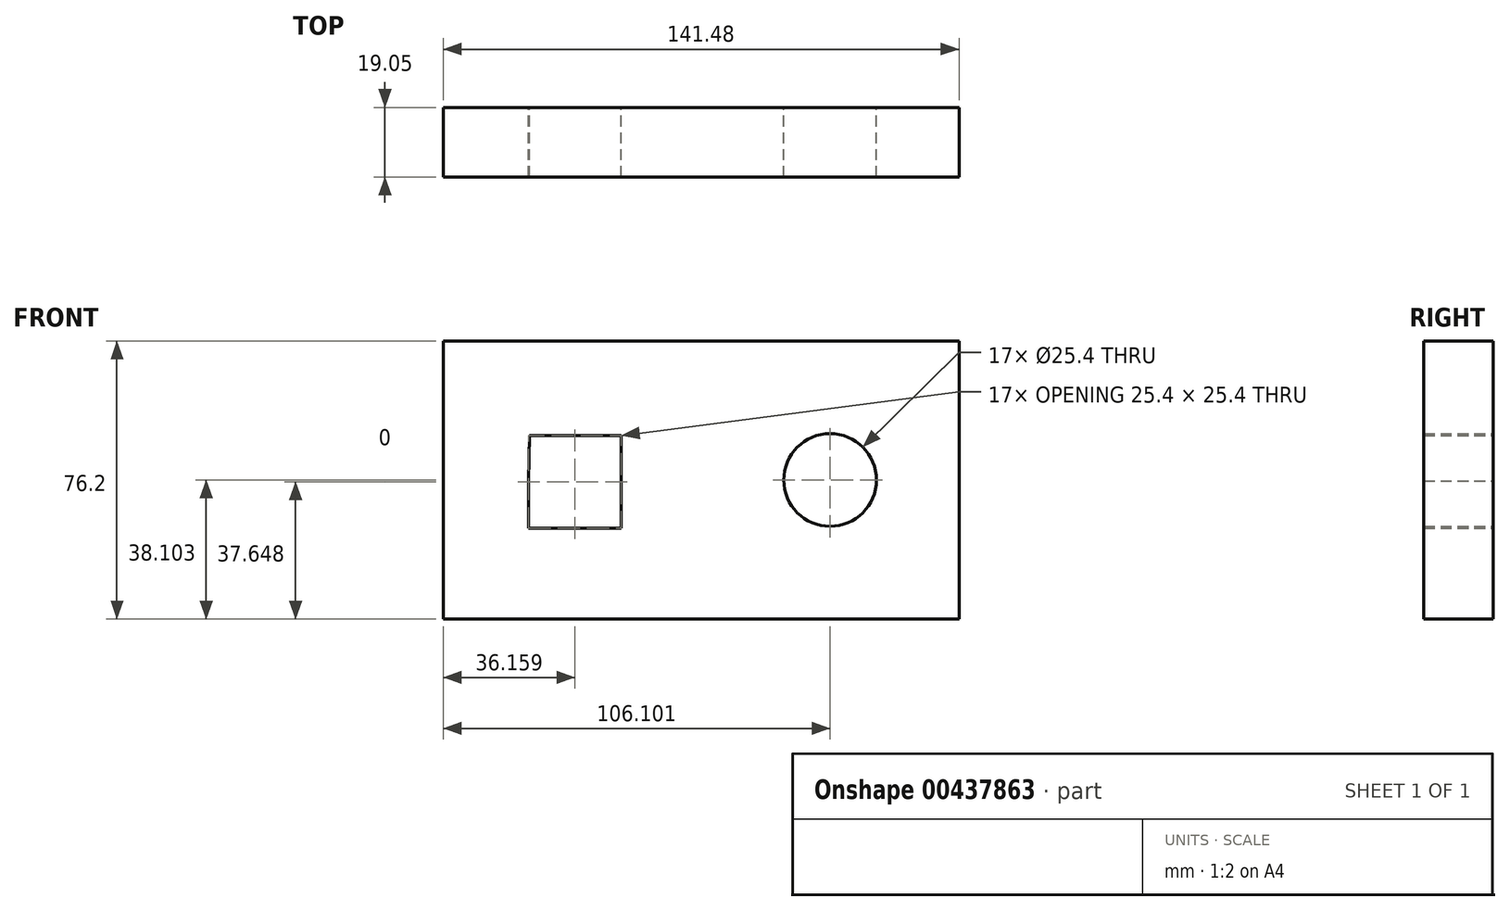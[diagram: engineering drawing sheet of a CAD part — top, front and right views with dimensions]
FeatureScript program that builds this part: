
annotation { "Feature Type Name" : "Feature", "Feature Type Description" : "" }
export const myFeature = defineFeature(function(context is Context, id is Id, definition is map)
    precondition{}
    {
        {
            var Q0;
            Q0=qCreatedBy(makeId("Front.planeOp"),FACE);
            var sketch = newSketch(context, id + "F0", { "sketchPlane" : qUnion([Q0])});
            skLineSegment(sketch, "E0", {"start": v(-73.29, 60.14) * mm, "end": v(68.2, 60.14) * mm});
            skPoint(sketch, "E1.start.orphan", {"position": v(-73.29, 47.35) * mm});
            skLineSegment(sketch, "E2", {"start": v(-73.29, 60.14) * mm, "end": v(-73.29, -16.06) * mm});
            skLineSegment(sketch, "E3", {"start": v(-73.29, -16.06) * mm, "end": v(-2.55, -16.06) * mm});
            skLineSegment(sketch, "E4", {"start": v(68.2, 60.14) * mm, "end": v(68.2, -16.06) * mm});
            skPoint(sketch, "E5.endSnap0", {"position": v(-3.02, -16.06) * mm});
            skPoint(sketch, "E6.end.orphan", {"position": v(-73.29, -21.4) * mm});
            skPoint(sketch, "E6.start.orphan", {"position": v(-2.55, -21.4) * mm});
            skPoint(sketch, "E7.orphan", {"position": v(-37.93, 0) * mm});
            skPoint(sketch, "E8.end.orphan", {"position": v(-40.56, 22.04) * mm});
            skPoint(sketch, "E9.trimOffspring.end.orphan", {"position": v(-73.29, 22.04) * mm});
            skPoint(sketch, "E10.end.orphan", {"position": v(-37.93, -21.4) * mm});
            skLineSegment(sketch, "E11", {"start": v(-37.13, 34.29) * mm, "end": v(-24.43, 34.29) * mm});
            skLineSegment(sketch, "E12", {"start": v(-24.43, 21.59) * mm, "end": v(-24.43, 34.29) * mm});
            skLineSegment(sketch, "E13", {"start": v(-37.13, 34.29) * mm, "end": v(-49.6, 34.29) * mm});
            skLineSegment(sketch, "E14", {"start": v(-49.83, 21.82) * mm, "end": v(-49.6, 34.29) * mm});
            skLineSegment(sketch, "E15", {"start": v(-37.13, 8.89) * mm, "end": v(-49.83, 8.89) * mm});
            skLineSegment(sketch, "E16", {"start": v(-49.83, 21.82) * mm, "end": v(-49.83, 8.89) * mm});
            skLineSegment(sketch, "E17", {"start": v(-24.43, 21.59) * mm, "end": v(-24.43, 8.89) * mm});
            skLineSegment(sketch, "E18", {"start": v(-37.13, 8.89) * mm, "end": v(-24.43, 8.89) * mm});
            skPoint(sketch, "E19.orphan", {"position": v(67.25, -16.06) * mm});
            skLineSegment(sketch, "E20", {"start": v(-2.55, -16.06) * mm, "end": v(68.2, -16.06) * mm});
            skCircle(sketch, "E21", {"center": v(32.81, 22.04) * mm, "radius": 12.7 * mm});
            skPoint(sketch, "E22.orphan", {"position": v(-2.55, 60.14) * mm});
            skPoint(sketch, "E23.orphan", {"position": v(68.2, 22.04) * mm});
            skSolve(sketch);
        }
        {
            var Q0;
            Q0=makeQuery(id+"F0.imprint","IMPRINT",FACE,{"disambiguationData":[TD([[makeQuery(id+"F0.imprint","IMPRINT",EDGE,{"derivedFrom":sQuery(id+"F0.wireOp",EDGE,"E0")}),-1.0]])]});
            extrude(context, id + "F1", {"entities" : qUnion([Q0]), "depth" : 19.05 * mm});
        }
    });
